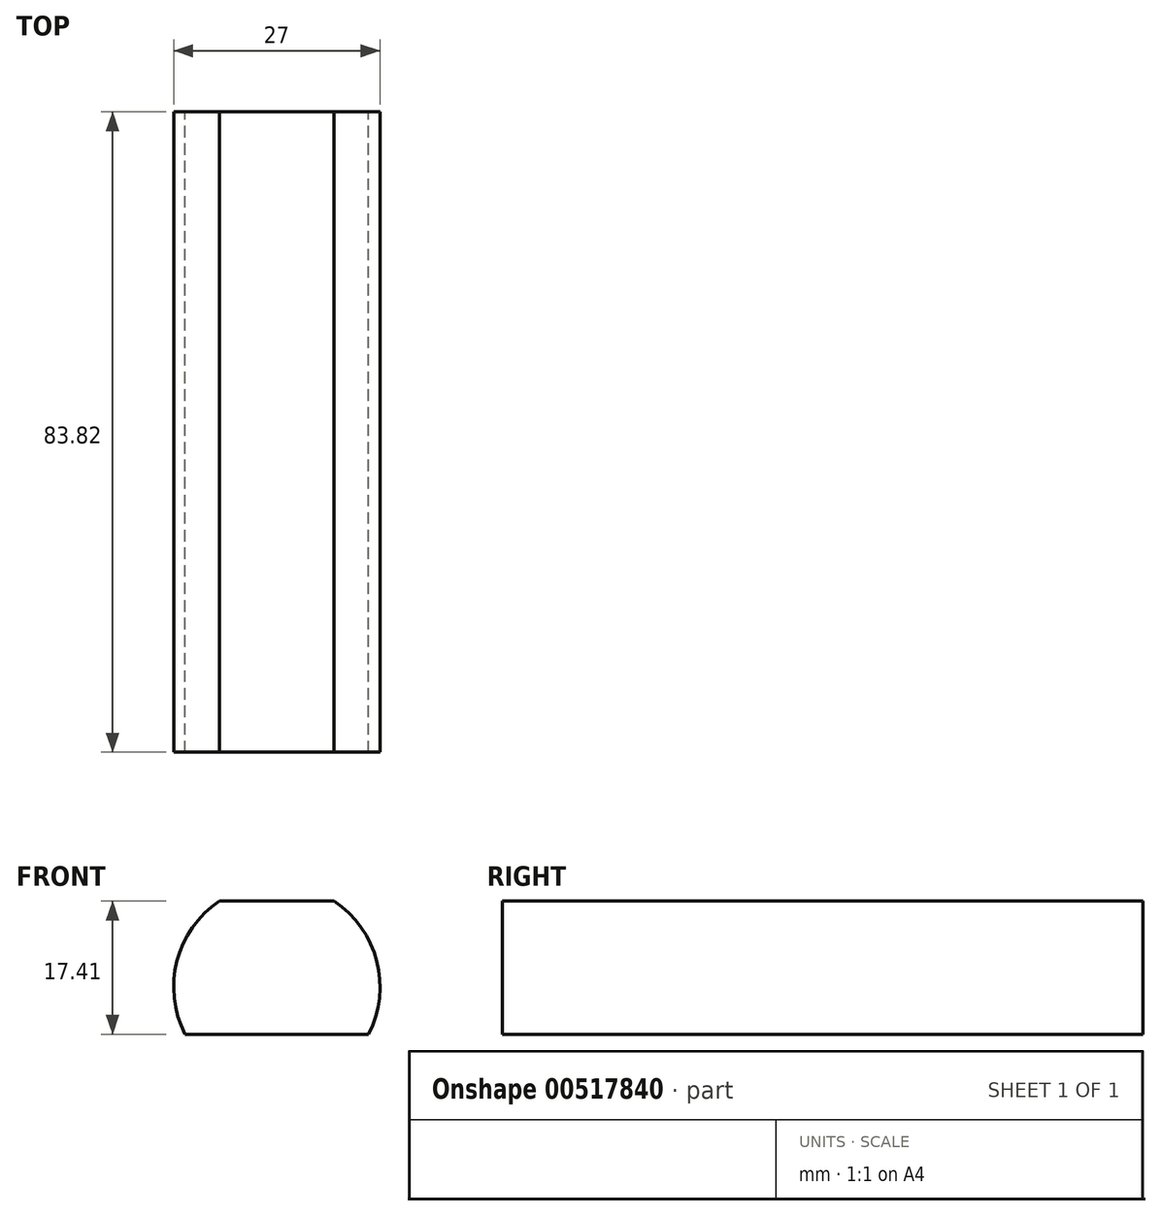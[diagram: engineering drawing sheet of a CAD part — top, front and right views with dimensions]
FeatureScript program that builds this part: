
annotation { "Feature Type Name" : "Feature", "Feature Type Description" : "" }
export const myFeature = defineFeature(function(context is Context, id is Id, definition is map)
    precondition{}
    {
        {
            var Q0;
            Q0=qCreatedBy(makeId("Front.planeOp"),FACE);
            var sketch = newSketch(context, id + "F0", { "sketchPlane" : qUnion([Q0])});
            skCircle(sketch, "E0", {"center": v(0, -0.51) * mm, "radius": 13.5 * mm});
            skArc(sketch, "E1", {"start": v(-7.5, 10.71) * mm, "mid": v(0, 13.08) * mm, "end": v(7.5, 10.71) * mm});
            skLineSegment(sketch, "E2", {"start": v(-7.5, 10.71) * mm, "end": v(7.5, 10.71) * mm});
            skArc(sketch, "E3", {"start": v(-12, -6.7) * mm, "mid": v(0, -13.74) * mm, "end": v(12, -6.7) * mm});
            skLineSegment(sketch, "E4", {"start": v(-12, -6.7) * mm, "end": v(12, -6.7) * mm});
            skSolve(sketch);
        }
        {
            var Q0;
            {var subQ0=sQuery(id+"F0.wireOp",EDGE,"E2");Q0=makeQuery(id+"F0.imprint","IMPRINT",FACE,{"disambiguationData":[TD([[makeQuery(id+"F0.imprint","IMPRINT",EDGE,{"derivedFrom":subQ0}),-1.0]])]});}
            extrude(context, id + "F1", {"entities" : qUnion([Q0]), "depth" : 83.82 * mm, "offsetDistance" : 25.4 * mm});
        }
    });
